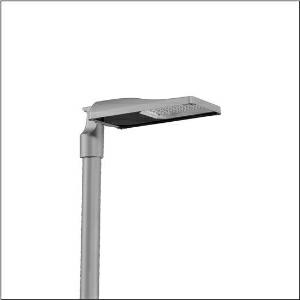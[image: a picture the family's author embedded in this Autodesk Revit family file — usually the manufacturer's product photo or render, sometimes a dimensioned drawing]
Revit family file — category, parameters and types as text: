
# Revit family: streetlight_sl_31_mini___st1_0a_5xh6d31b08ga_f949
name_source: partatom
category: Lighting Fixtures
units: mm (PartAtom-declared; Revit-internal decimal feet)

## family parameters
Cut with Voids When Loaded = No
Host = Face
Light Source = No
Part Type = Normal
Room Calculation Point = No
Round Connector Dimension = Use Diameter
Shared = No

## types (1)
- --- (1 x LED, 5710 lm, 37.3 W, 3000K)
    Apparent Load = 37 VA
    CIE Flux Codes = 37 72 97 100 100
    Color Rendering = 70
    Color Temperature = 3000K
    Default Elevation = 1800 mm
    Description = Streetlight SL 31 mini Easy, LST, Desk-Remote mast luminaire for post-top, side-entry; light control with lens of PMMA; light distribution: ST1.0a, direct asymmetric distribution, for standard-compliant lighting for roads and squares; LED: luminous flux: 5.710lm, light colour: 730, colour temperature: 3000K; luminous efficacy: 153,1lm/W; control: pre-setting: linear dimming characteristic, flexible luminous flux parameterisation, time-dependent luminous flux control, constant luminous flux control, power reduction, intelligent temperature release in ECG and LED module, overheat protection; luminaire housing, of diecast aluminium, Siteco® metallic grey (DB 702S), corrosivity category C5 high according to DIN EN ISO 12944; cover of toughened safety glass, transparent, opened without tools; mast flange of diecast aluminium, Siteco® metallic grey (DB 702S), spigot size: 76/60mm, mast flange included unmounted; with cable H07RN-F 3x 1.5mm², cable length: 6,5m, connection cable pre-assembled; mains connection: 220..240V, AC, 50/60Hz; power consumption (at start of service life): 37,3W / (at end of service life): 38,7W / (with reduced operation 50%): 17,5W; protection rating (complete): IP66; insulation class (complete): insulation class II (safety insulation); impact resistance: IK10; certification: CE, ENEC, ENEC+, VDE, UKCA; permissible operating ambient temperature for outdoor applications: -40..+50°C; packaging unit: 1 piece

Light Distribution: ST1.0a
    Height = 76 mm
    Lamp = 1 x LED
    Lamp Light Flux = 5710 lm
    Lamp Power = 37.3 W
    Lamp count = 1
    Length = 547 mm
    Luminous efficacy = 153 lm/W
    Manufacturer = Siteco
    ModVariant = No
    Model = 5XH6D31B08GA
    Number of Poles = 1
    OnlyDefault = Yes
    Power Factor = 1
    Product Name = Streetlight SL 31 mini | ST1.0a
    Product group = mast luminaire | pylon top
    ProductGroupID = 6100
    Protection Class = Protection class II
    Protection Degree = IP 66
    RLX_Detail_Level = 1
    RLX_Emergency_Light_Flux = 0 lm
    RLX_Emergency_Type = 0
    RLX_Emergency_Type_DB = No
    RlxData = <blob elided: 39685 chars, md5=bf803e47>
    Socket = socket
    Standby Power = 0 W
    System Light Flux = 5710 lm
    System Power = 37 W
    Type Comments = factory setting: luminous flux: 100 % | dim-lin: 254 | 386 mA
    Type Image = l_1300326.jpg
    URL = http://relux.com
    VarID = @adj_054232
    Voltage = 0 V
    Weight = 0.00 kg
    Width = 265 mm

## geometry (parser evidence)
native form markers: Blend x4, Sweep x9
no freeform markers — native parametric forms only
